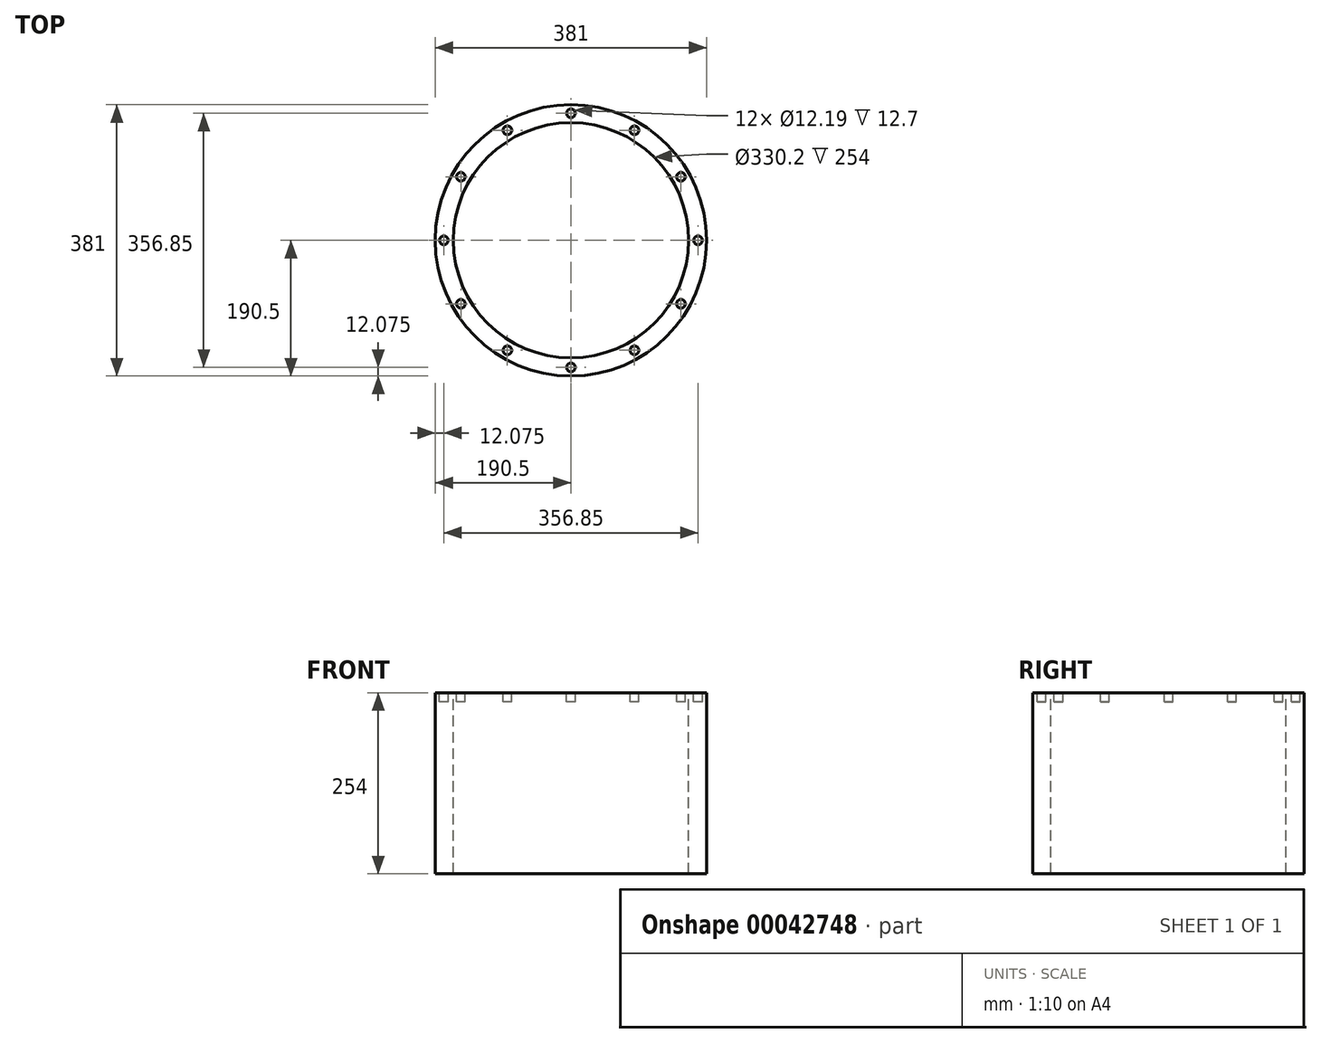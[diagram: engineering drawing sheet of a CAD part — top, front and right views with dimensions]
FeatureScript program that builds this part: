
annotation { "Feature Type Name" : "Feature", "Feature Type Description" : "" }
export const myFeature = defineFeature(function(context is Context, id is Id, definition is map)
    precondition{}
    {
        {
            var Q0;
            Q0=qCreatedBy(makeId("Top.planeOp"),FACE);
            var sketch = newSketch(context, id + "F0", { "sketchPlane" : qUnion([Q0])});
            skCircle(sketch, "E0", {"center": v(0, 0) * mm, "radius": 190.5 * mm});
            skCircle(sketch, "E1", {"center": v(0, 0) * mm, "radius": 165.1 * mm});
            skSolve(sketch);
        }
        {
            var Q0;
            Q0 = qSketchRegion(id + "F0", true);
            var Q1;
            Q1 = qConstructionFilter(qBodyType(qCreatedBy(id + "F0" ,EDGE), BodyType.WIRE), ConstructionObject.NO);
            extrude(context, id + "F1", {"entities" : qUnion([Q0]), "surfaceEntities" : qUnion([Q1]), "oppositeDirection" : true, "depth" : 254 * mm});
        }
        {
            var Q0;
            Q0=qCreatedBy(makeId("Top.planeOp"),FACE);
            var sketch = newSketch(context, id + "F2", { "sketchPlane" : qUnion([Q0])});
            skCircle(sketch, "E2", {"center": v(0, 178.42) * mm, "radius": 6.1 * mm});
            skCircle(sketch, "E3", {"center": v(0, 0) * mm, "radius": 178.42 * mm, "construction": true});
            skCircle(sketch, "E4.1.0", {"center": v(-89.21, 154.52) * mm, "radius": 6.1 * mm});
            skCircle(sketch, "E4.2.0", {"center": v(-154.52, 89.21) * mm, "radius": 6.1 * mm});
            skCircle(sketch, "E4.3.0", {"center": v(-178.42, 0) * mm, "radius": 6.1 * mm});
            skCircle(sketch, "E4.4.0", {"center": v(-154.52, -89.21) * mm, "radius": 6.1 * mm});
            skCircle(sketch, "E4.5.0", {"center": v(-89.21, -154.52) * mm, "radius": 6.1 * mm});
            skCircle(sketch, "E4.6.0", {"center": v(0, -178.42) * mm, "radius": 6.1 * mm});
            skCircle(sketch, "E4.7.0", {"center": v(89.21, -154.52) * mm, "radius": 6.1 * mm});
            skCircle(sketch, "E4.8.0", {"center": v(154.52, -89.21) * mm, "radius": 6.1 * mm});
            skCircle(sketch, "E4.9.0", {"center": v(178.42, 0) * mm, "radius": 6.1 * mm});
            skCircle(sketch, "E4.10.0", {"center": v(154.52, 89.21) * mm, "radius": 6.1 * mm});
            skCircle(sketch, "E4.11.0", {"center": v(89.21, 154.52) * mm, "radius": 6.1 * mm});
            skSolve(sketch);
        }
        {
            var Q0;
            Q0 = qSketchRegion(id + "F2", true);
            extrude(context, id + "F3", {"entities" : qUnion([Q0]), "operationType" : NewBodyOperationType.REMOVE, "oppositeDirection" : true, "depth" : 12.7 * mm});
        }
    });
